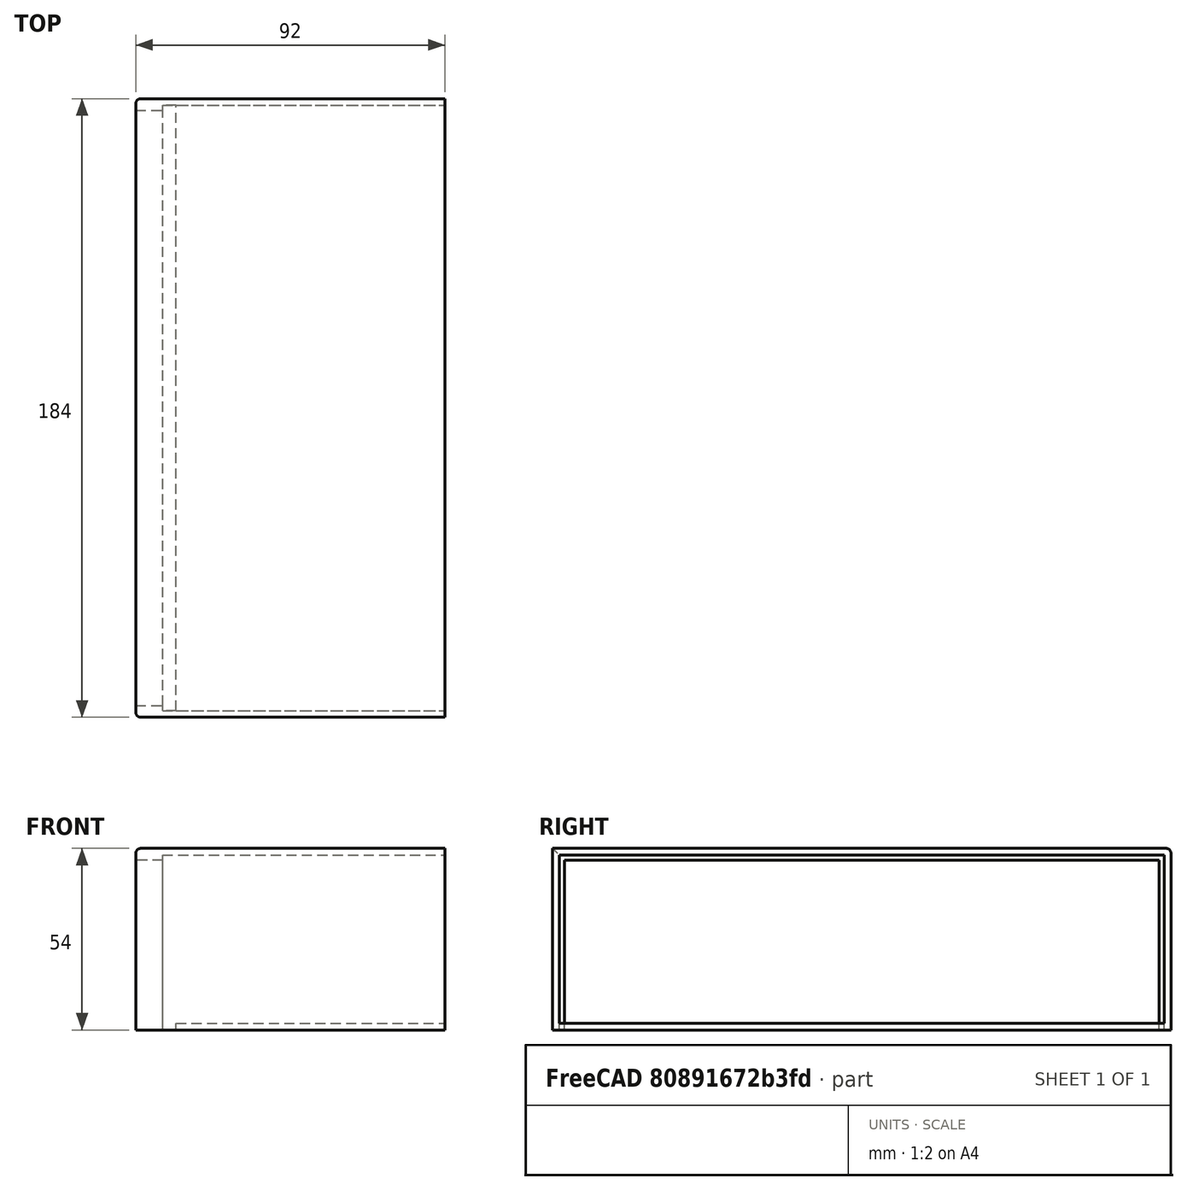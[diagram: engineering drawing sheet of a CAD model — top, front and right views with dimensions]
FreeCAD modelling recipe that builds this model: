
FCSTD DOCUMENT  (FreeCAD 0.21R33771 (Git))
Label: subaru-dash
License: All rights reserved
LicenseURL: http://en.wikipedia.org/wiki/All_rights_reserved
objects: Part::Box×6, Part::Cut×2, Part::MultiFuse×1, Part::Fillet×1
note: 10 computed .brp shape members not serialized (recipe doc carries the construction recipe); baked Part::Feature solids carry a one-line shape summary decoded from their .brp

FEATURE [Part::Box] Box  label="Cube"
  AttacherType = Attacher::AttachEngine3D
  Height = 50
  Length = 160
  Width = 180
FEATURE [Part::Box] Box001  label="Cube001"
  AttacherType = Attacher::AttachEngine3D
  Height = 54
  Length = 92
  Placement = pos=(0,-2,-2) rot=(0,0,1;0rad)
  Width = 184
FEATURE [Part::Box] Box002  label="Cube002"
  AttacherType = Attacher::AttachEngine3D
  Height = 52
  Length = 12
  Placement = pos=(0,0,-20) rot=(0,0,1;0rad)
  Width = 180
FEATURE [Part::Cut] Cut
  Base = -> Box001
  Tool = -> Box
FEATURE [Part::Cut] Cut001
  Base = -> Cut
  Tool = -> Box002
FEATURE [Part::Box] Box003  label="Cube003"
  AttacherType = Attacher::AttachEngine3D
  Height = 1.5
  Length = 8
  Placement = pos=(0,0,48.5) rot=(0,0,1;0rad)
  Width = 180
FEATURE [Part::Box] Box004  label="Cube004"
  AttacherType = Attacher::AttachEngine3D
  Height = 52
  Length = 8
  Placement = pos=(0,0,-2) rot=(0,0,1;0rad)
  Width = 1.5
FEATURE [Part::Box] Box005  label="Cube005"
  AttacherType = Attacher::AttachEngine3D
  Height = 52
  Length = 8
  Placement = pos=(0,178.5,-2) rot=(0,0,1;0rad)
  Width = 1.5
FEATURE [Part::MultiFuse] Fusion
  Shapes = -> [Cut001,Box003,Box004,Box005]
FEATURE [Part::Fillet] Fillet  label="draft"
  Base = -> Fusion
  Edges = 4 edges r=1.5: [Edge5,Edge6,Edge18,Edge23]
